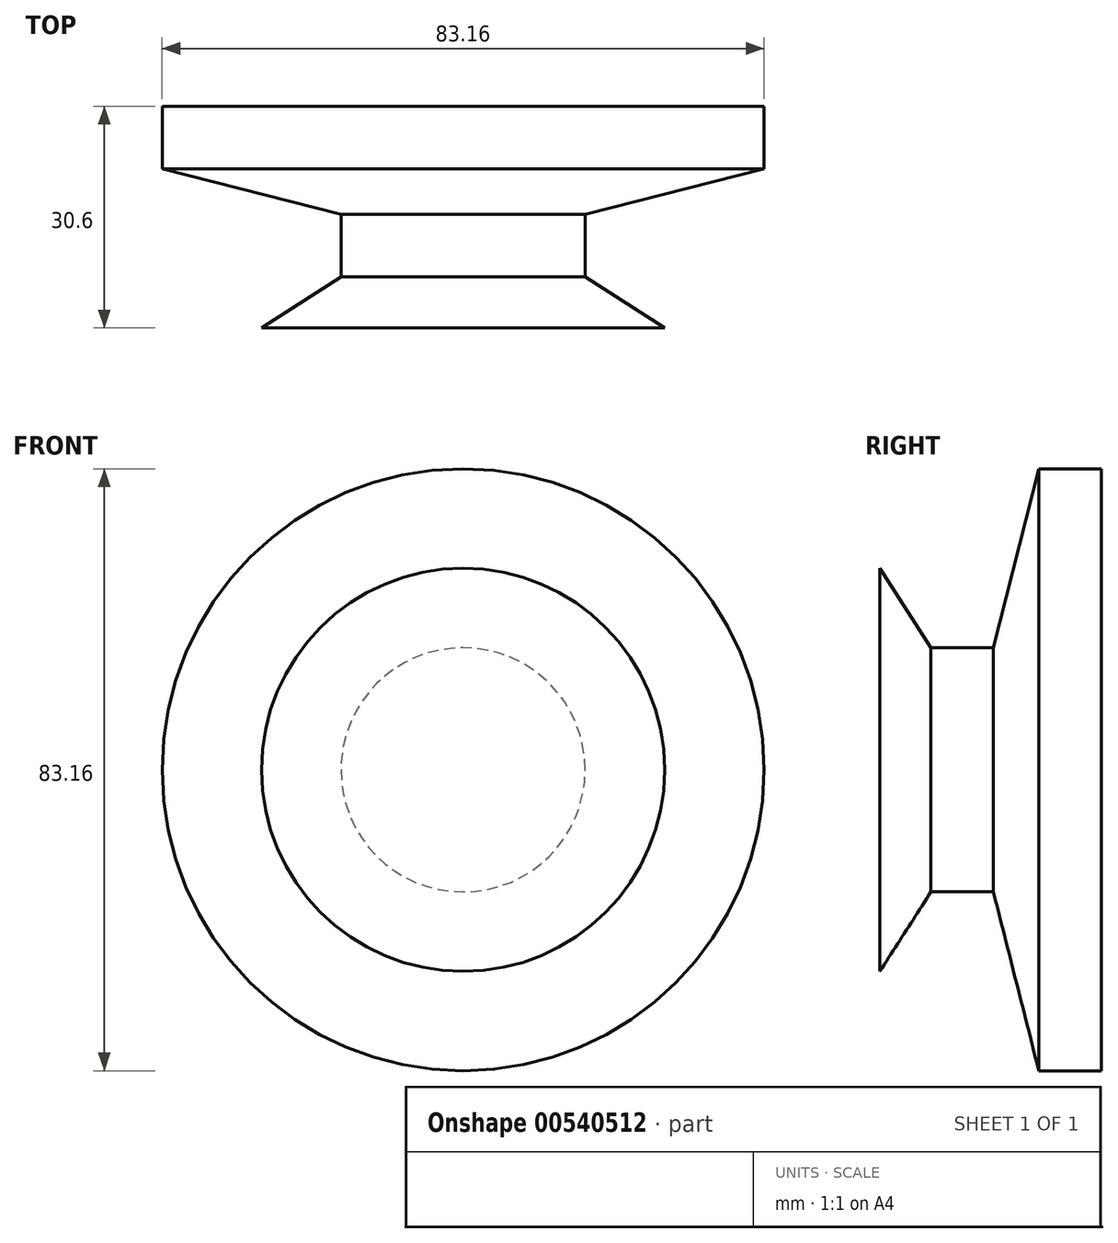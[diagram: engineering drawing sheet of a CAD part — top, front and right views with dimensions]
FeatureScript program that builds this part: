
annotation { "Feature Type Name" : "Feature", "Feature Type Description" : "" }
export const myFeature = defineFeature(function(context is Context, id is Id, definition is map)
    precondition{}
    {
        {
            var Q0;
            Q0=qCreatedBy(makeId("Top.planeOp"),FACE);
            var sketch = newSketch(context, id + "F0", { "sketchPlane" : qUnion([Q0])});
            skLineSegment(sketch, "E0", {"start": v(0, 0) * mm, "end": v(0, 30.6) * mm});
            skLineSegment(sketch, "E1", {"start": v(0, 30.6) * mm, "end": v(-41.58, 30.6) * mm});
            skLineSegment(sketch, "E2", {"start": v(-41.58, 30.6) * mm, "end": v(-41.58, 21.97) * mm});
            skLineSegment(sketch, "E3", {"start": v(-41.58, 21.97) * mm, "end": v(-16.87, 15.69) * mm});
            skLineSegment(sketch, "E4", {"start": v(-16.87, 15.69) * mm, "end": v(-16.87, 7.06) * mm});
            skLineSegment(sketch, "E5", {"start": v(-16.87, 7.06) * mm, "end": v(-27.85, 0) * mm});
            skLineSegment(sketch, "E6", {"start": v(0, 0) * mm, "end": v(-27.85, 0) * mm});
            skSolve(sketch);
        }
        {
            var Q0;
            Q0 = qSketchRegion(id + "F0", true);
            var Q1;
            Q1=sQuery(id+"F0.wireOp",EDGE,"E0");
            revolve(context, id + "F1", {"entities" : qUnion([Q0]), "axis" : qUnion([Q1]), "revolveType" : RevolveType.FULL});
        }
    });
